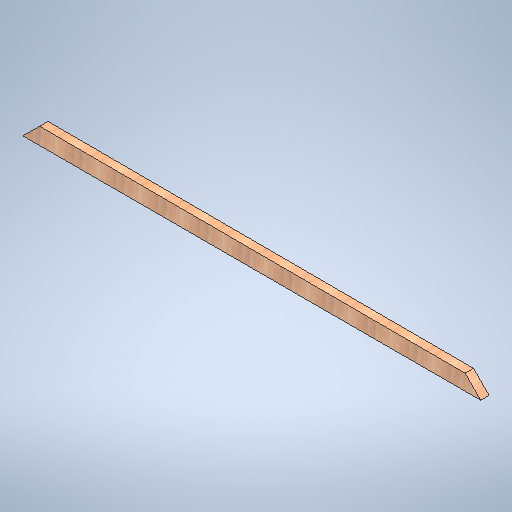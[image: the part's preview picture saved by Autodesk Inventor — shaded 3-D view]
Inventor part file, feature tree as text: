
AUTODESK INVENTOR PART (.ipt)
format: ipt  version: 2025 (Build 290162000, 162)  size: 284,160 bytes
history: native  units: in
note: dims shown in document units (in); Inventor stores cm internally (conversion verified against a paired STEP export)
features: extrude x1, sketch x1
ambient origin geometry x8: Origin, YZ Plane, XZ Plane, XY Plane, X Axis, Y Axis, Z Axis, Center Point
bodies: Solid1 (feature_tree)
feature tree (2):
  extrude  "Extrusion1"  Depth=2.0in TaperAngle=0.0deg
  sketch  "Sketch1"  dims[d0=4.0in d1=2.0in d2=0.0in]
